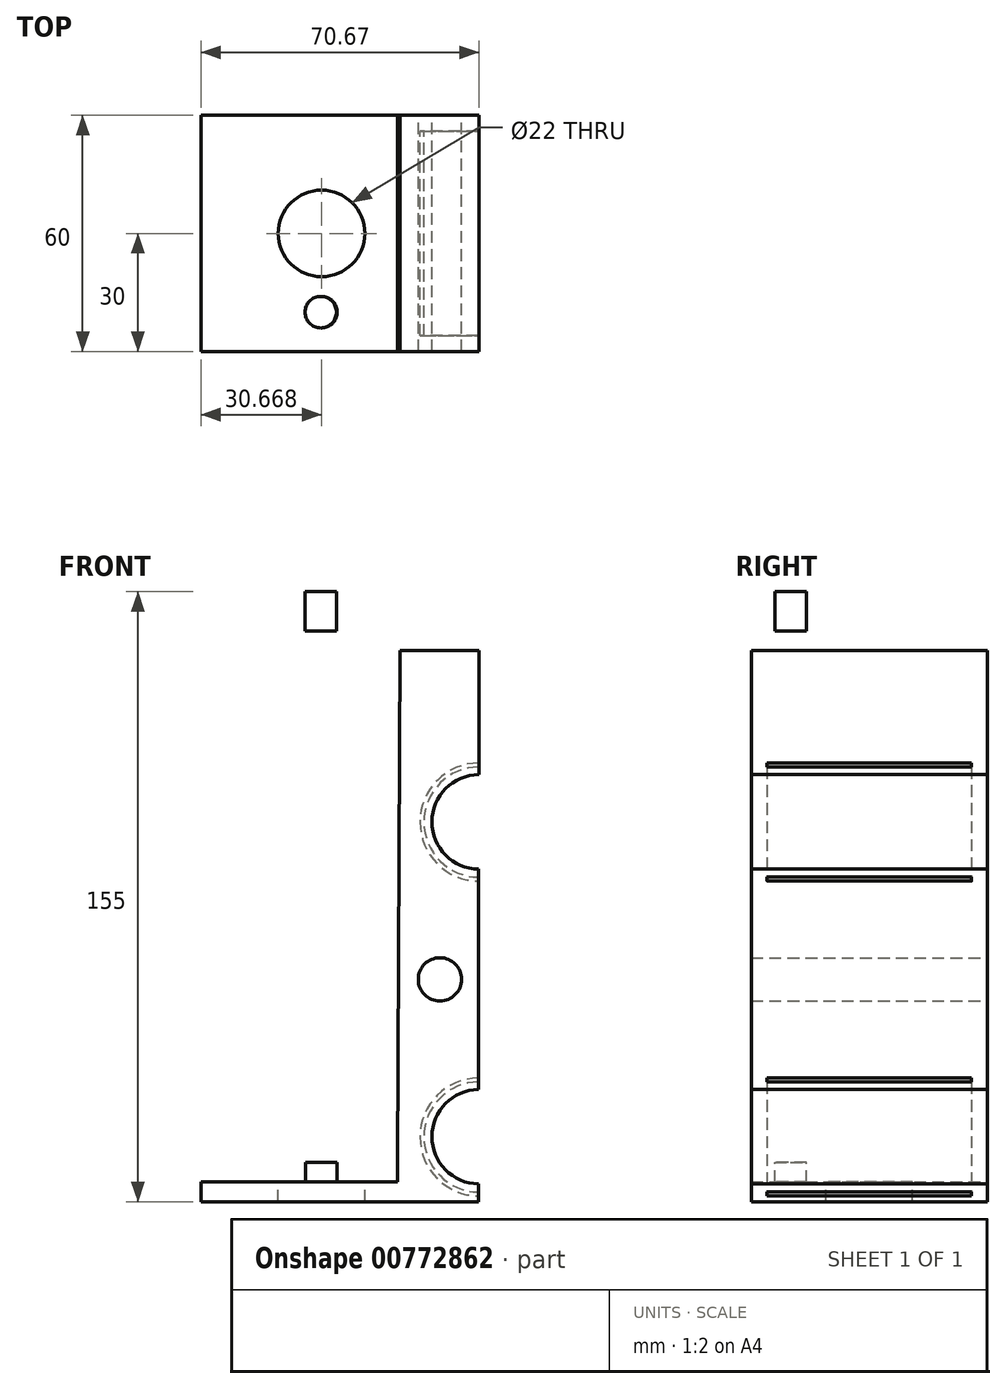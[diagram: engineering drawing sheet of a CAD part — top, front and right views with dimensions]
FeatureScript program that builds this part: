
annotation { "Feature Type Name" : "Feature", "Feature Type Description" : "" }
export const myFeature = defineFeature(function(context is Context, id is Id, definition is map)
    precondition{}
    {
        {
            var Q0;
            Q0=qCreatedBy(makeId("Front.planeOp"),FACE);
            var sketch = newSketch(context, id + "F0", { "sketchPlane" : qUnion([Q0])});
            skCircle(sketch, "E0", {"center": v(0, -41.48) * mm, "radius": 7.25 * mm});
            skCircle(sketch, "E1.MirrorC", {"center": v(0, -121.48) * mm, "radius": 7.25 * mm});
            skArc(sketch, "E2", {"start": v(0, -30.48) * mm, "mid": v(-11, -41.48) * mm, "end": v(0, -52.48) * mm});
            skArc(sketch, "E3", {"start": v(0, -29.48) * mm, "mid": v(-12, -41.48) * mm, "end": v(0, -53.48) * mm});
            skArc(sketch, "E4.MirrorCS", {"start": v(0, -133.46) * mm, "mid": v(-12, -121.46) * mm, "end": v(0, -109.46) * mm});
            skArc(sketch, "E5.MirrorCS", {"start": v(0, -132.47) * mm, "mid": v(-11, -121.47) * mm, "end": v(0, -110.47) * mm});
            skLineSegment(sketch, "E6", {"start": v(-70.04, 7.04) * mm, "end": v(-20.04, 7.04) * mm});
            skLineSegment(sketch, "E7", {"start": v(-70.7, -127.96) * mm, "end": v(-20.7, -127.96) * mm});
            skLineSegment(sketch, "E8", {"start": v(-20.04, 7.04) * mm, "end": v(-20.7, -127.96) * mm});
            skLineSegment(sketch, "E9", {"start": v(-0.2, -137.96) * mm, "end": v(0, 17.04) * mm});
            skLineSegment(sketch, "E10", {"start": v(-70.04, 7.04) * mm, "end": v(-70.04, 17.04) * mm});
            skLineSegment(sketch, "E11", {"start": v(0, 17.04) * mm, "end": v(-70.04, 17.04) * mm});
            skLineSegment(sketch, "E12", {"start": v(-70.7, -127.96) * mm, "end": v(-70.7, -137.96) * mm});
            skLineSegment(sketch, "E13", {"start": v(-0.2, -137.96) * mm, "end": v(-70.7, -137.96) * mm});
            skCircle(sketch, "E14", {"center": v(-9.95, -81.48) * mm, "radius": 5.5 * mm});
            skPoint(sketch, "E14.centerSnap0", {"position": v(-0.1, -81.48) * mm});
            skSolve(sketch);
        }
        {
            var Q0;
            Q0=makeQuery(id+"F0.imprint","IMPRINT",FACE,{"disambiguationData":[TD([[makeQuery(id+"F0.imprint","IMPRINT",EDGE,{"derivedFrom":sQuery(id+"F0.wireOp",EDGE,"E6")}),1.0]])]});
            extrude(context, id + "F1", {"entities" : qUnion([Q0]), "depth" : 60 * mm, "offsetDistance" : 25 * mm});
        }
        {
            var Q0;
            Q0=makeQuery(id+"F1.opExtrude","SWEPT_BODY",BODY,{"disambiguationData":[OSD([sQuery(id+"F0.wireOp",EDGE,"E0"),sQuery(id+"F0.wireOp",EDGE,"E1.MirrorC"),sQuery(id+"F0.wireOp",EDGE,"E6"),sQuery(id+"F0.wireOp",EDGE,"E7"),sQuery(id+"F0.wireOp",EDGE,"E8"),sQuery(id+"F0.wireOp",EDGE,"E9"),sQuery(id+"F0.wireOp",EDGE,"E10"),sQuery(id+"F0.wireOp",EDGE,"E11"),sQuery(id+"F0.wireOp",EDGE,"E12"),sQuery(id+"F0.wireOp",EDGE,"E13")])]});
            transform(context, id + "F2", {"entities" : qUnion([Q0]), "transformType" : TransformType.TRANSLATION_3D, "dx" : 0 * mm, "dy" : 30 * mm, "dz" : 0 * mm, "makeCopy" : false});
        }
        {
            var Q0;
            Q0=qCreatedBy(makeId("Front.planeOp"),FACE);
            var sketch = newSketch(context, id + "F3", { "sketchPlane" : qUnion([Q0])});
            skArc(sketch, "E15", {"start": v(0, -27.52) * mm, "mid": v(-14, -41.52) * mm, "end": v(0, -55.52) * mm});
            skArc(sketch, "E16", {"start": v(0, -26.52) * mm, "mid": v(-15, -41.52) * mm, "end": v(0, -56.52) * mm});
            skLineSegment(sketch, "E17", {"start": v(0, -56.52) * mm, "end": v(0, -55.52) * mm});
            skLineSegment(sketch, "E18", {"start": v(0, -27.52) * mm, "end": v(0, -26.52) * mm});
            skLineSegment(sketch, "E19.MirrorCS", {"start": v(0, -106.52) * mm, "end": v(0, -107.52) * mm});
            skLineSegment(sketch, "E20.MirrorCS", {"start": v(0, -135.52) * mm, "end": v(0, -136.52) * mm});
            skArc(sketch, "E21.MirrorCS", {"start": v(0, -135.52) * mm, "mid": v(-14, -121.52) * mm, "end": v(0, -107.52) * mm});
            skArc(sketch, "E22.MirrorCS", {"start": v(0, -136.52) * mm, "mid": v(-15, -121.52) * mm, "end": v(0, -106.52) * mm});
            skSolve(sketch);
        }
        {
            var Q0;
            Q0=makeQuery(id+"F3.imprint","IMPRINT",FACE,{"disambiguationData":[TD([[makeQuery(id+"F3.imprint","IMPRINT",EDGE,{"derivedFrom":sQuery(id+"F3.wireOp",EDGE,"dad4a0fd-5b9c-4c14-b859-4023bab104060.MirrorCS")}),-1.0]])]});
            var Q1;
            Q1=makeQuery(id+"F3.imprint","IMPRINT",FACE,{"disambiguationData":[TD([[makeQuery(id+"F3.imprint","IMPRINT",EDGE,{"derivedFrom":sQuery(id+"F3.wireOp",EDGE,"E15")}),-1.0]])]});
            var Q2;
            Q2=makeQuery(id+"F3.imprint","IMPRINT",FACE,{"disambiguationData":[TD([[makeQuery(id+"F3.imprint","IMPRINT",EDGE,{"derivedFrom":sQuery(id+"F3.wireOp",EDGE,"E19.MirrorCS")}),-1.0]])]});
            extrude(context, id + "F4", {"entities" : qUnion([Q0, Q1, Q2]), "operationType" : NewBodyOperationType.REMOVE, "depth" : 26 * mm, "offsetDistance" : 25 * mm, "hasSecondDirection" : true, "secondDirectionOppositeDirection" : true, "secondDirectionDepth" : 26 * mm});
        }
        {
            var Q0;
            Q0=makeQuery(id+"F1.opExtrude","SWEPT_FACE",FACE,{"disambiguationData":[OSD([sQuery(id+"F0.wireOp",EDGE,"E7")])]});
            var sketch = newSketch(context, id + "F5", { "sketchPlane" : qUnion([Q0])});
            skCircle(sketch, "E23", {"center": v(-40.04, 20) * mm, "radius": 4 * mm});
            skCircle(sketch, "E24.MirrorC", {"center": v(-40.04, -20) * mm, "radius": 4 * mm});
            skSolve(sketch);
        }
        {
            var Q0;
            Q0=makeQuery(id+"F5.imprint","IMPRINT",FACE,{"disambiguationData":[TD([[makeQuery(id+"F5.imprint","IMPRINT",EDGE,{"derivedFrom":sQuery(id+"F5.wireOp",EDGE,"E24.MirrorC")}),-1.0]])]});
            var Q1;
            Q1=makeQuery(id+"F5.imprint","IMPRINT",FACE,{"disambiguationData":[TD([[makeQuery(id+"F5.imprint","IMPRINT",EDGE,{"derivedFrom":sQuery(id+"F5.wireOp",EDGE,"E23")}),1.0]])]});
            var Q2;
            Q2=sQuery(id+"F5.wireOp",EDGE,"E23");
            var Q3;
            Q3=sQuery(id+"F5.wireOp",EDGE,"E24.MirrorC");
            extrude(context, id + "F6", {"entities" : qUnion([Q0, Q1]), "operationType" : NewBodyOperationType.REMOVE, "surfaceEntities" : qUnion([Q2, Q3]), "oppositeDirection" : true, "depth" : 5 * mm, "offsetDistance" : 25 * mm});
        }
        {
            var Q0;
            Q0=makeQuery(id+"F1.opExtrude","SWEPT_FACE",FACE,{"disambiguationData":[OSD([sQuery(id+"F0.wireOp",EDGE,"E11")])]});
            var sketch = newSketch(context, id + "F7", { "sketchPlane" : qUnion([Q0])});
            skCircle(sketch, "E25", {"center": v(-40.04, 20) * mm, "radius": 4 * mm});
            skCircle(sketch, "E26.MirrorC", {"center": v(-40.23, -20) * mm, "radius": 4 * mm});
            skSolve(sketch);
        }
        {
            var Q0;
            Q0=makeQuery(id+"F7.imprint","IMPRINT",FACE,{"disambiguationData":[TD([[makeQuery(id+"F7.imprint","IMPRINT",EDGE,{"derivedFrom":sQuery(id+"F7.wireOp",EDGE,"E25")}),1.0]])]});
            var Q1;
            Q1=makeQuery(id+"F7.imprint","IMPRINT",FACE,{"disambiguationData":[TD([[makeQuery(id+"F7.imprint","IMPRINT",EDGE,{"derivedFrom":sQuery(id+"F7.wireOp",EDGE,"E26.MirrorC")}),-1.0]])]});
            extrude(context, id + "F8", {"entities" : qUnion([Q0, Q1]), "operationType" : NewBodyOperationType.REMOVE, "oppositeDirection" : true, "depth" : 15 * mm, "offsetDistance" : 25 * mm});
        }
        {
            var Q0;
            Q0=makeQuery(id+"F1.opExtrude","SWEPT_FACE",FACE,{"disambiguationData":[OSD([sQuery(id+"F0.wireOp",EDGE,"E7")])]});
            var sketch = newSketch(context, id + "F9", { "sketchPlane" : qUnion([Q0])});
            skCircle(sketch, "E27", {"center": v(-40.02, 0) * mm, "radius": 11 * mm});
            skSolve(sketch);
        }
        {
            var Q0;
            Q0=makeQuery(id+"F9.imprint","IMPRINT",FACE,{"disambiguationData":[TD([[makeQuery(id+"F9.imprint","IMPRINT",EDGE,{"derivedFrom":sQuery(id+"F9.wireOp",EDGE,"E27")}),1.0]])]});
            extrude(context, id + "F10", {"entities" : qUnion([Q0]), "operationType" : NewBodyOperationType.REMOVE, "endBound" : BoundingType.THROUGH_ALL, "oppositeDirection" : true, "depth" : 25 * mm, "offsetDistance" : 25 * mm});
        }
        {
            var Q0;
            Q0=makeQuery(id+"F1.opExtrude","SWEPT_FACE",FACE,{"disambiguationData":[OSD([sQuery(id+"F0.wireOp",EDGE,"E11")])]});
            var sketch = newSketch(context, id + "F11", { "sketchPlane" : qUnion([Q0])});
            skCircle(sketch, "E28", {"center": v(-40.02, 0) * mm, "radius": 6 * mm});
            skSolve(sketch);
        }
        {
            var Q0;
            Q0=makeQuery(id+"F11.imprint","IMPRINT",FACE,{"disambiguationData":[TD([[makeQuery(id+"F11.imprint","IMPRINT",EDGE,{"derivedFrom":sQuery(id+"F11.wireOp",EDGE,"E28")}),1.0]])]});
            extrude(context, id + "F12", {"entities" : qUnion([Q0]), "operationType" : NewBodyOperationType.REMOVE, "oppositeDirection" : true, "depth" : 25 * mm, "offsetDistance" : 25 * mm});
        }
    });
